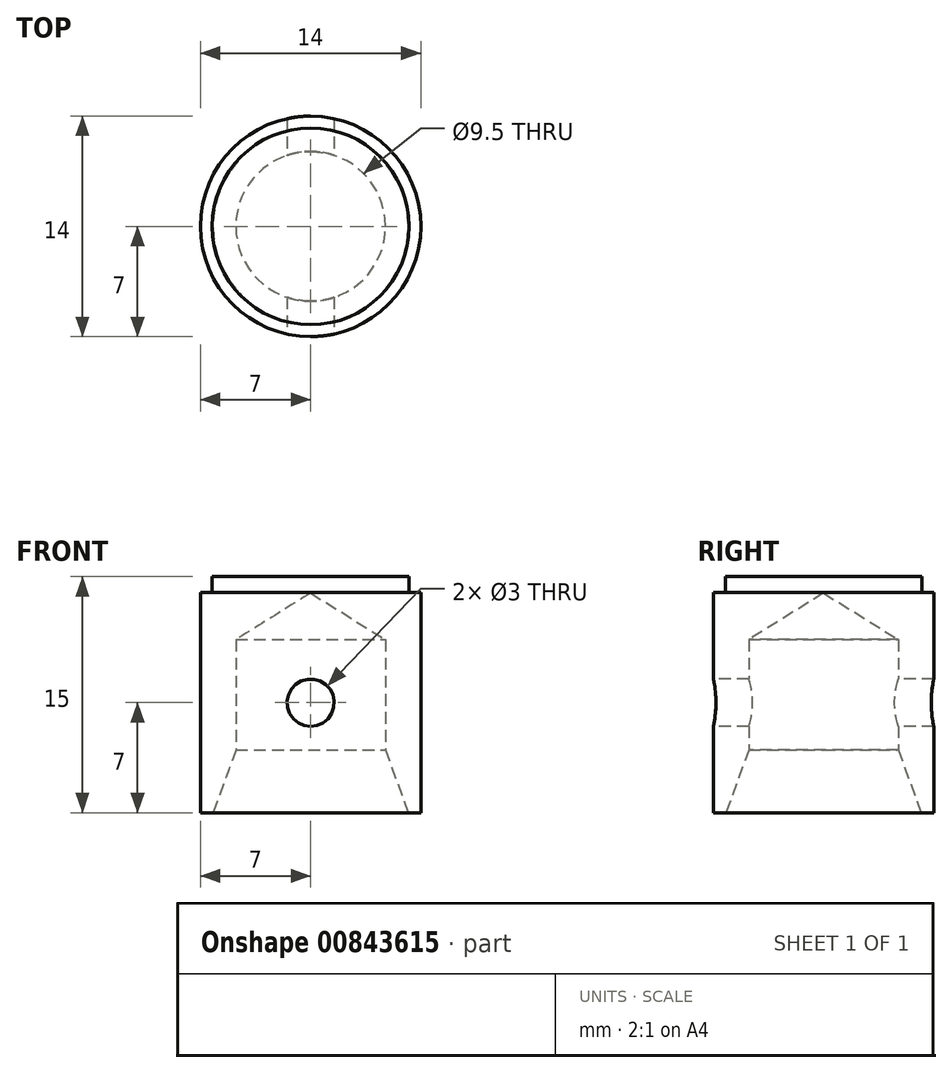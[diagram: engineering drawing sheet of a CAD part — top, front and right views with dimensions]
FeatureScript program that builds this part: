
annotation { "Feature Type Name" : "Feature", "Feature Type Description" : "" }
export const myFeature = defineFeature(function(context is Context, id is Id, definition is map)
    precondition{}
    {
        {
            var Q0;
            Q0=qCreatedBy(makeId("Top.planeOp"),FACE);
            var sketch = newSketch(context, id + "F0", { "sketchPlane" : qUnion([Q0])});
            skCircle(sketch, "E0", {"center": v(0, 0) * mm, "radius": 6.25 * mm});
            skSolve(sketch);
        }
        {
            var Q0;
            Q0 = qSketchRegion(id + "F0", true);
            extrude(context, id + "F1", {"entities" : qUnion([Q0]), "oppositeDirection" : true, "depth" : 1 * mm, "offsetDistance" : 25 * mm});
        }
        {
            var Q0;
            Q0=makeQuery(id+"F1.opExtrude","CAP_FACE",FACE,{"disambiguationData":[OSD([sQuery(id+"F0.wireOp",EDGE,"E0")])],"isStart":false});
            var sketch = newSketch(context, id + "F2", { "sketchPlane" : qUnion([Q0])});
            skCircle(sketch, "E1", {"center": v(0, 0) * mm, "radius": 7 * mm});
            skSolve(sketch);
        }
        {
            var Q0;
            Q0 = qSketchRegion(id + "F2", true);
            extrude(context, id + "F3", {"entities" : qUnion([Q0]), "operationType" : NewBodyOperationType.ADD, "depth" : 14 * mm, "offsetDistance" : 25 * mm});
        }
        {
            var Q0;
            Q0=qCreatedBy(makeId("Right.planeOp"),FACE);
            var sketch = newSketch(context, id + "F4", { "sketchPlane" : qUnion([Q0])});
            skLineSegment(sketch, "E2", {"start": v(0, -1.04) * mm, "end": v(-4.75, -4) * mm});
            skLineSegment(sketch, "E3", {"start": v(-4.75, -4) * mm, "end": v(-4.75, -11.02) * mm});
            skLineSegment(sketch, "E4", {"start": v(-4.75, -11.02) * mm, "end": v(-6.2, -15) * mm});
            skLineSegment(sketch, "E5", {"start": v(-6.2, -15) * mm, "end": v(0, -15) * mm});
            skLineSegment(sketch, "E6", {"start": v(0, -15) * mm, "end": v(0, -1.04) * mm});
            skSolve(sketch);
        }
        {
            var Q0;
            Q0 = qSketchRegion(id + "F4", true);
            var Q1;
            Q1=makeQuery(id+"F3.opExtrude","CAP_EDGE",EDGE,{"disambiguationData":[OSD([sQuery(id+"F2.wireOp",EDGE,"E1")])],"isStart":false});
            revolve(context, id + "F5", {"operationType" : NewBodyOperationType.REMOVE, "surfaceOperationType" : NewSurfaceOperationType.NEW, "entities" : qUnion([Q0]), "axis" : qUnion([Q1]), "revolveType" : RevolveType.FULL, "oppositeDirection" : true});
        }
        {
            var Q0;
            Q0=qCreatedBy(makeId("Front.planeOp"),FACE);
            var sketch = newSketch(context, id + "F6", { "sketchPlane" : qUnion([Q0])});
            skCircle(sketch, "E7", {"center": v(0, -8) * mm, "radius": 1.5 * mm});
            skSolve(sketch);
        }
        {
            var Q0;
            Q0 = qSketchRegion(id + "F6", true);
            extrude(context, id + "F7", {"entities" : qUnion([Q0]), "operationType" : NewBodyOperationType.REMOVE, "oppositeDirection" : true, "depth" : 25 * mm, "offsetDistance" : 25 * mm, "symmetric" : true});
        }
    });
